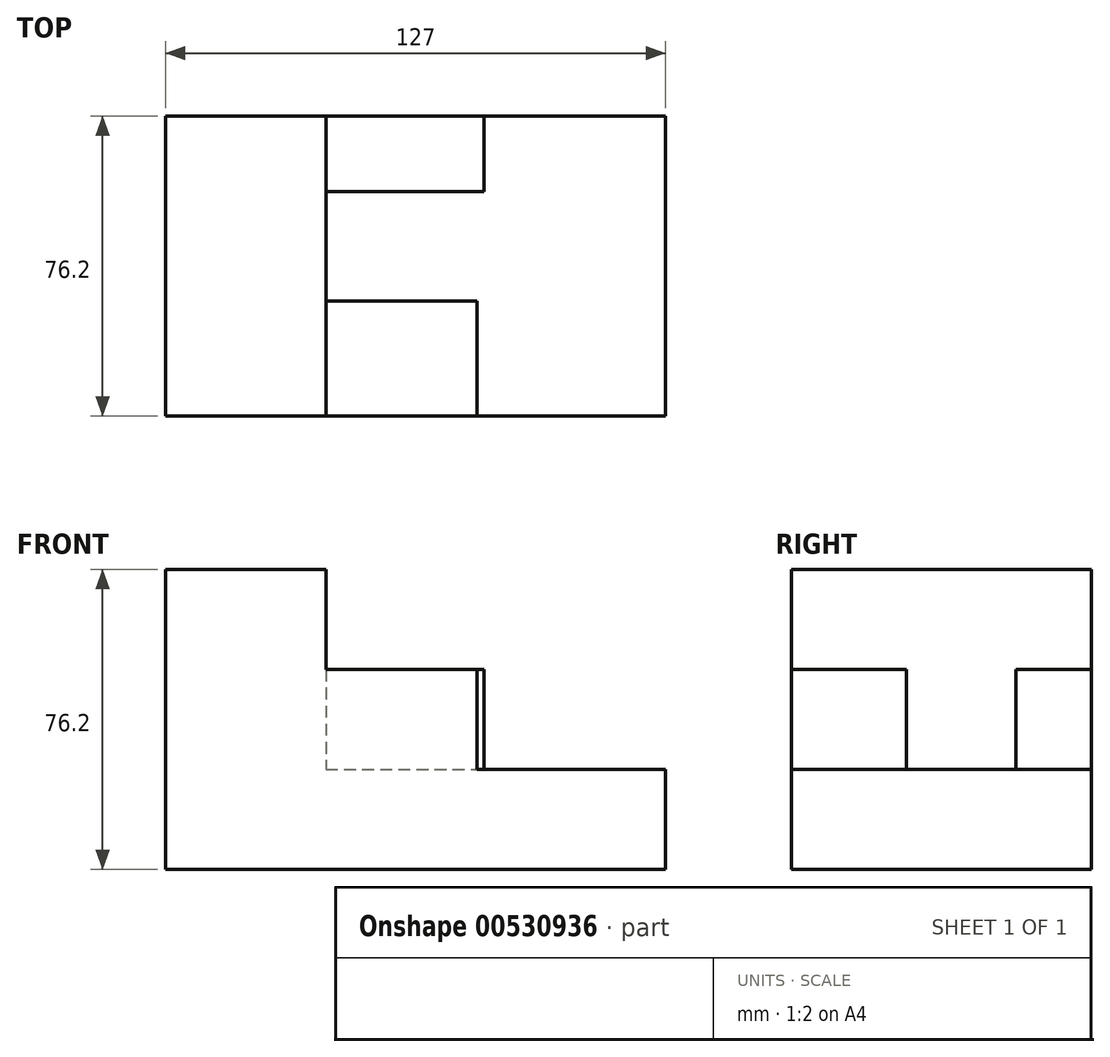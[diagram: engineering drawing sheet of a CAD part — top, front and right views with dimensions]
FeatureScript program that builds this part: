
annotation { "Feature Type Name" : "Feature", "Feature Type Description" : "" }
export const myFeature = defineFeature(function(context is Context, id is Id, definition is map)
    precondition{}
    {
        {
            var Q0;
            Q0=qCreatedBy(makeId("Top.planeOp"),FACE);
            var sketch = newSketch(context, id + "F0", { "sketchPlane" : qUnion([Q0])});
            skLineSegment(sketch, "E0.bottom", {"start": v(63.5, -38.1) * mm, "end": v(-63.5, -38.1) * mm});
            skLineSegment(sketch, "E0.top", {"start": v(63.5, 38.1) * mm, "end": v(-63.5, 38.1) * mm});
            skLineSegment(sketch, "E0.left", {"start": v(63.5, -38.1) * mm, "end": v(63.5, 38.1) * mm});
            skLineSegment(sketch, "E0.right", {"start": v(-63.5, -38.1) * mm, "end": v(-63.5, 38.1) * mm});
            skPoint(sketch, "E0.middle", {"position": v(0, 0) * mm});
            skSolve(sketch);
        }
        {
            var Q0;
            Q0=makeQuery(id+"F0.imprint","IMPRINT",FACE,{"disambiguationData":[TD([[makeQuery(id+"F0.imprint","IMPRINT",EDGE,{"derivedFrom":sQuery(id+"F0.wireOp",EDGE,"E0.bottom")}),-1.0]])]});
            extrude(context, id + "F1", {"entities" : qUnion([Q0]), "depth" : 25.4 * mm, "offsetDistance" : 25.4 * mm});
        }
        {
            var Q0;
            Q0=makeQuery(id+"F1.opExtrude","CAP_FACE",FACE,{"disambiguationData":[OSD([sQuery(id+"F0.wireOp",EDGE,"E0.bottom"),sQuery(id+"F0.wireOp",EDGE,"E0.top"),sQuery(id+"F0.wireOp",EDGE,"E0.left"),sQuery(id+"F0.wireOp",EDGE,"E0.right")])],"isStart":false});
            var sketch = newSketch(context, id + "F2", { "sketchPlane" : qUnion([Q0])});
            skLineSegment(sketch, "E1.bottom", {"start": v(-63.5, 38.1) * mm, "end": v(-22.75, 38.1) * mm});
            skLineSegment(sketch, "E1.top", {"start": v(-63.5, -38.1) * mm, "end": v(-22.75, -38.1) * mm});
            skLineSegment(sketch, "E1.left", {"start": v(-63.5, 38.1) * mm, "end": v(-63.5, -38.1) * mm});
            skLineSegment(sketch, "E1.right", {"start": v(-22.75, 38.1) * mm, "end": v(-22.75, -38.1) * mm});
            skSolve(sketch);
        }
        {
            var Q0;
            Q0=makeQuery(id+"F2.imprint","IMPRINT",FACE,{"disambiguationData":[TD([[makeQuery(id+"F2.imprint","IMPRINT",EDGE,{"derivedFrom":sQuery(id+"F2.wireOp",EDGE,"E1.bottom")}),1.0]])]});
            extrude(context, id + "F3", {"entities" : qUnion([Q0]), "operationType" : NewBodyOperationType.ADD, "depth" : 50.8 * mm, "offsetDistance" : 25.4 * mm});
        }
        {
            var Q0;
            Q0=makeQuery(id+"F1.opExtrude","CAP_FACE",FACE,{"disambiguationData":[OSD([sQuery(id+"F0.wireOp",EDGE,"E0.bottom"),sQuery(id+"F0.wireOp",EDGE,"E0.top"),sQuery(id+"F0.wireOp",EDGE,"E0.left"),sQuery(id+"F0.wireOp",EDGE,"E0.right")])],"isStart":false});
            var sketch = newSketch(context, id + "F4", { "sketchPlane" : qUnion([Q0])});
            skLineSegment(sketch, "E2.bottom", {"start": v(-22.75, 38.1) * mm, "end": v(17.39, 38.1) * mm});
            skLineSegment(sketch, "E2.top", {"start": v(-22.75, 18.9) * mm, "end": v(17.39, 18.9) * mm});
            skLineSegment(sketch, "E2.left", {"start": v(-22.75, 38.1) * mm, "end": v(-22.75, 18.9) * mm});
            skLineSegment(sketch, "E2.right", {"start": v(17.39, 38.1) * mm, "end": v(17.39, 18.9) * mm});
            skSolve(sketch);
        }
        {
            var Q0;
            Q0=makeQuery(id+"F4.imprint","IMPRINT",FACE,{"disambiguationData":[TD([[makeQuery(id+"F4.imprint","IMPRINT",EDGE,{"derivedFrom":sQuery(id+"F4.wireOp",EDGE,"E2.bottom")}),1.0]])]});
            extrude(context, id + "F5", {"entities" : qUnion([Q0]), "operationType" : NewBodyOperationType.ADD, "depth" : 25.4 * mm, "offsetDistance" : 25.4 * mm});
        }
        {
            var Q0;
            Q0=makeQuery(id+"F1.opExtrude","CAP_FACE",FACE,{"disambiguationData":[OSD([sQuery(id+"F0.wireOp",EDGE,"E0.bottom"),sQuery(id+"F0.wireOp",EDGE,"E0.top"),sQuery(id+"F0.wireOp",EDGE,"E0.left"),sQuery(id+"F0.wireOp",EDGE,"E0.right")])],"isStart":false});
            var sketch = newSketch(context, id + "F6", { "sketchPlane" : qUnion([Q0])});
            skLineSegment(sketch, "E3.bottom", {"start": v(-22.75, -38.1) * mm, "end": v(15.59, -38.1) * mm});
            skLineSegment(sketch, "E3.top", {"start": v(-22.75, -8.85) * mm, "end": v(15.59, -8.85) * mm});
            skLineSegment(sketch, "E3.left", {"start": v(-22.75, -38.1) * mm, "end": v(-22.75, -8.85) * mm});
            skLineSegment(sketch, "E3.right", {"start": v(15.59, -38.1) * mm, "end": v(15.59, -8.85) * mm});
            skSolve(sketch);
        }
        {
            var Q0;
            Q0=makeQuery(id+"F6.imprint","IMPRINT",FACE,{"disambiguationData":[TD([[makeQuery(id+"F6.imprint","IMPRINT",EDGE,{"derivedFrom":sQuery(id+"F6.wireOp",EDGE,"E3.bottom")}),-1.0]])]});
            extrude(context, id + "F7", {"entities" : qUnion([Q0]), "operationType" : NewBodyOperationType.ADD, "depth" : 25.4 * mm, "offsetDistance" : 25.4 * mm});
        }
    });
